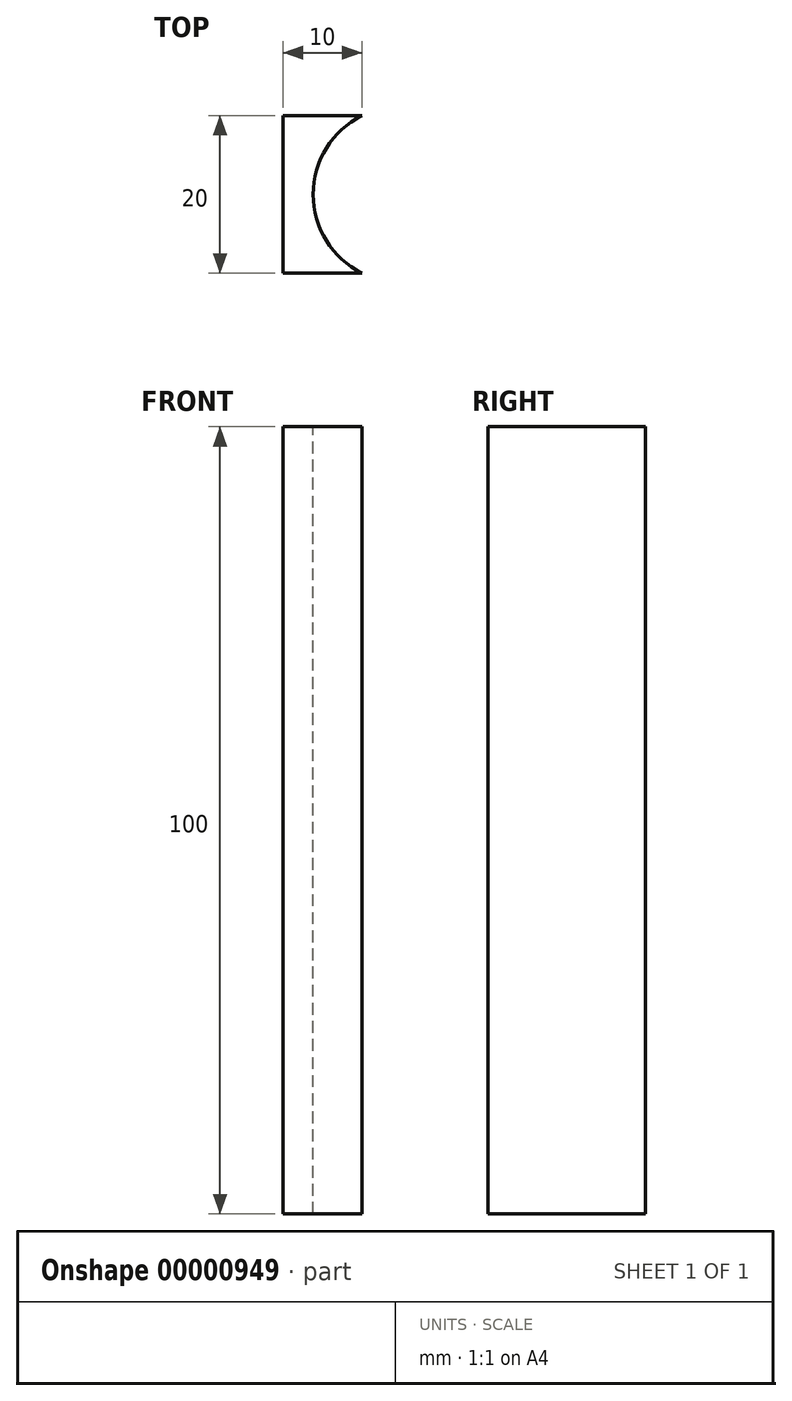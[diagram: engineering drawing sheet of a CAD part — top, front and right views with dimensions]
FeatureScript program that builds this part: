
annotation { "Feature Type Name" : "Feature", "Feature Type Description" : "" }
export const myFeature = defineFeature(function(context is Context, id is Id, definition is map)
    precondition{}
    {
        {
            var Q0;
            Q0=qCreatedBy(makeId("Front.planeOp"),FACE);
            var sketch = newSketch(context, id + "F0", { "sketchPlane" : qUnion([Q0])});
            skLineSegment(sketch, "E0.bottom", {"start": v(0, 0) * mm, "end": v(20, 0) * mm});
            skLineSegment(sketch, "E0.top", {"start": v(0, 100) * mm, "end": v(20, 100) * mm});
            skLineSegment(sketch, "E0.left", {"start": v(0, 0) * mm, "end": v(0, 100) * mm});
            skLineSegment(sketch, "E0.right", {"start": v(20, 0) * mm, "end": v(20, 100) * mm});
            skSolve(sketch);
        }
        {
            var Q0;
            Q0=makeQuery(id+"F0.imprint","IMPRINT",FACE,{"disambiguationData":[TD([[makeQuery(id+"F0.imprint","IMPRINT",EDGE,{"derivedFrom":sQuery(id+"F0.wireOp",EDGE,"E0.bottom")}),1.0]])]});
            extrude(context, id + "F1", {"entities" : qUnion([Q0]), "depth" : 20 * mm});
        }
        {
            var Q0;
            Q0=makeQuery(id+"F1.opExtrude","SWEPT_FACE",FACE,{"disambiguationData":[OSD([sQuery(id+"F0.wireOp",EDGE,"E0.top")])]});
            var sketch = newSketch(context, id + "F2", { "sketchPlane" : qUnion([Q0])});
            skCircle(sketch, "E1", {"center": v(15, -10) * mm, "radius": 11.18 * mm});
            skPoint(sketch, "E1.first.point", {"position": v(20, -20) * mm});
            skPoint(sketch, "E1.second.point", {"position": v(20, 0) * mm});
            skPoint(sketch, "E1.third.point", {"position": v(10, 0) * mm});
            skSolve(sketch);
        }
        {
            var Q0;
            {var subQ0=sQuery(id+"F0.wireOp",EDGE,"E0.top");var subQ1=makeQuery(id+"F1.opExtrude","SWEPT_EDGE",EDGE,{"disambiguationData":[OSD([subQ0,sQuery(id+"F0.wireOp",EDGE,"E0.right")])]});var subQ2=makeQuery(id+"F2.imprint","IMPRINT",EDGE,{"derivedFrom":subQ1});var subQ3=sQuery(id+"F2.wireOp",EDGE,"E1");var subQ4=makeQuery(id+"F1.opExtrude","CAP_EDGE",EDGE,{"disambiguationData":[OSD([subQ0])],"isStart":false});var subQ6=makeQuery(id+"F1.opExtrude","CAP_EDGE",EDGE,{"disambiguationData":[OSD([subQ0])],"isStart":true});var subQ8=makeQuery(id+"F2.imprint","INTERSECT",VERTEX,{"derivedFrom":[subQ6,subQ3]});var subQ10=makeQuery(id+"F2.imprint","INTERSECT",VERTEX,{"derivedFrom":[subQ4,subQ3]});Q0=qUnion([makeQuery(id+"F2.imprint","IMPRINT",FACE,{"disambiguationData":[TD([[subQ2,-1.0]])]}),makeQuery(id+"F2.imprint","IMPRINT",FACE,{"disambiguationData":[TD([[makeQuery(id+"F2.imprint","IMPRINT",EDGE,{"disambiguationData":[TD([[subQ8,1.0]])],"derivedFrom":subQ3}),1.0]])]}),makeQuery(id+"F2.imprint","IMPRINT",FACE,{"disambiguationData":[TD([[makeQuery(id+"F2.imprint","IMPRINT",EDGE,{"disambiguationData":[TD([[subQ10,-1.0]])],"derivedFrom":subQ3}),1.0]])]}),makeQuery(id+"F2.imprint","IMPRINT",FACE,{"disambiguationData":[TD([[subQ2,1.0]])]})]);}
            extrude(context, id + "F3", {"entities" : qUnion([Q0]), "operationType" : NewBodyOperationType.REMOVE, "endBound" : BoundingType.UP_TO_NEXT, "oppositeDirection" : true, "depth" : 25 * mm});
        }
    });
